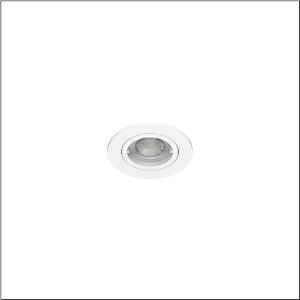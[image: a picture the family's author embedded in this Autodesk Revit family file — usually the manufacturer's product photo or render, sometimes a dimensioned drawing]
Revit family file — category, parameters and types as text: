
# Revit family: lunis_41_spot_51dt137a32a
name_source: partatom
category: Lighting Fixtures
units: mm (PartAtom-declared; Revit-internal decimal feet)

## family parameters
Cut with Voids When Loaded = No
Host = Face
Light Source = No
Part Type = Normal
Room Calculation Point = No
Round Connector Dimension = Use Diameter
Shared = No

## types (1)
- Lunis 41 Spot (1 x LED, 650 lm, 6.5 W, 3000K)
    Apparent Load = 7 VA
    CIE Flux Codes = 87 97 99 100 100
    Color Rendering = 80
    Color Temperature = 3000K
    Default Elevation = 1800 mm
    Description = Lunis 41,  Spot, downlight, light emission: direct distribution, LED rated luminous flux: 650lm, light colour: 830, control gear: ECG, mains connection: 230V, AC, 50/60Hz, housing, round, of aluminium, coated, traffic white (RAL 9016), diameter: 88mm, recess depth: 54mm, protection rating (complete): IP20, protection rating (on room side): IP20, insulation class (complete): insulation class II (safety insulation), certification: CE, permissible ambient temperature for indoor applications: -20..+40°C, packaging unit: 1 piece
    Height = 0 mm  [stored 0 ft]
    Lamp = 1 x LED
    Lamp Light Flux = 650 lm
    Lamp Power = 6.5 W
    Lamp count = 1
    Length = 88 mm
    Luminous efficacy = 100 lm/W
    Manufacturer = Siteco
    ModVariant = No
    Model = 51DT137A32A
    Mounting Place = Ceiling
    Mounting Type = Recessed
    Number of Poles = 1
    OnlyDefault = Yes
    Power Factor = 1
    Product Name = Lunis 41 Spot
    Product group = downlight
    ProductGroupID = 400
    Protection Class = Protection class II
    Protection Degree = IP 20
    RLX_Detail_Level = 1
    RLX_Emergency_Light_Flux = 0 lm
    RLX_Emergency_Type = 0
    RLX_Emergency_Type_DB = No
    RlxData = <blob elided: 38033 chars, md5=2ae2e62c>
    Socket = socket
    Standby Power = 0 W
    System Light Flux = 650 lm
    System Power = 7 W
    Type Comments = Product without accessories
    Type Image = l_1005286.jpg
    URL = http://relux.com
    VarID = ---
    Voltage = 0 V
    Weight = 0.00 kg
    Width = 0 mm  [stored 0 ft]

note: [stored X ft] marks values corroborated as IEEE doubles in the binary element streams (Revit-internal decimal feet)

## geometry (parser evidence)
native form markers: Blend x4, Sweep x9
no freeform markers — native parametric forms only
